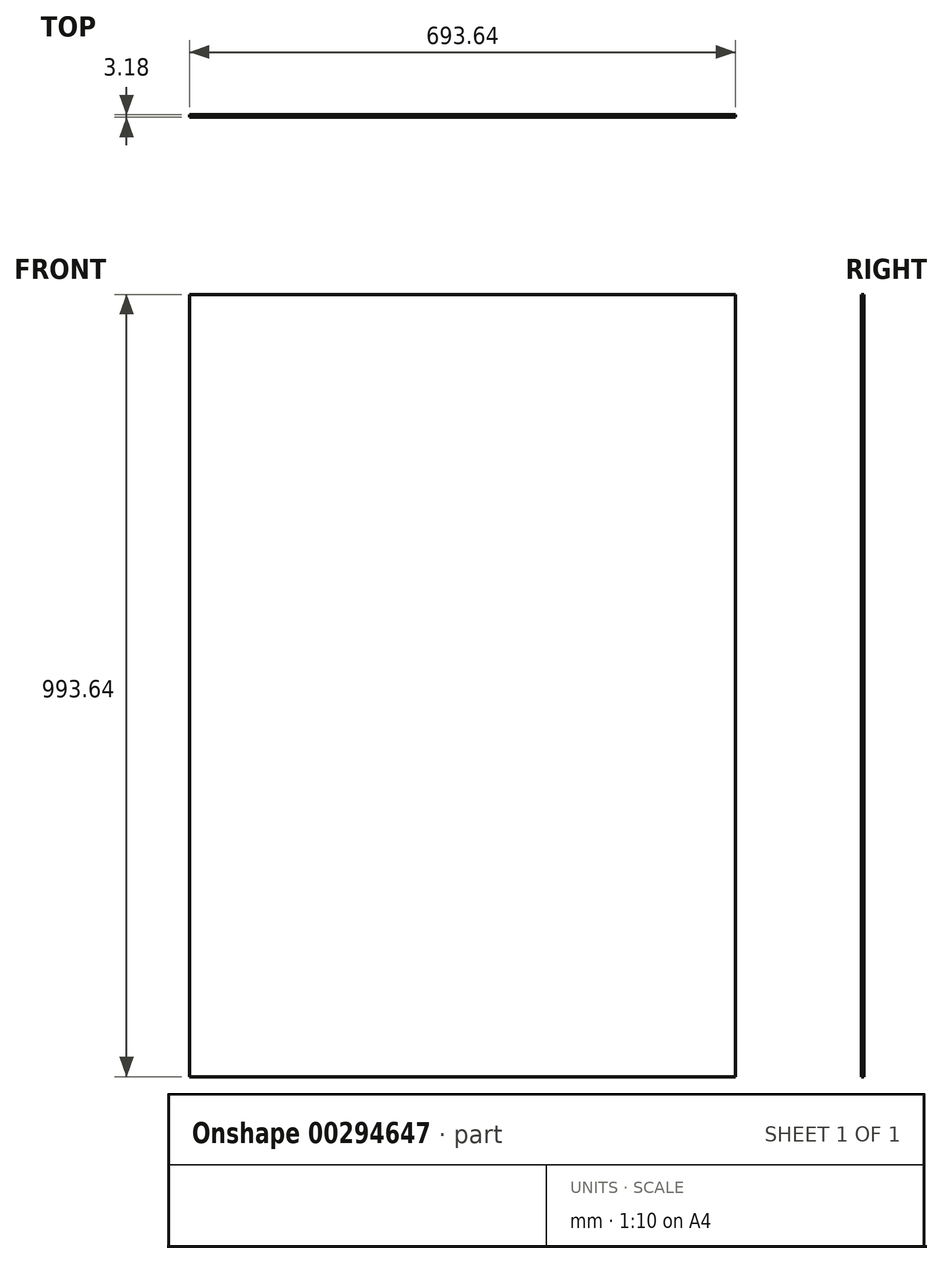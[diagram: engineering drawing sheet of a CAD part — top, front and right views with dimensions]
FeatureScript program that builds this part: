
annotation { "Feature Type Name" : "Feature", "Feature Type Description" : "" }
export const myFeature = defineFeature(function(context is Context, id is Id, definition is map)
    precondition{}
    {
        {
            var Q0;
            Q0=qCreatedBy(makeId("Front.planeOp"),FACE);
            var sketch = newSketch(context, id + "F0", { "sketchPlane" : qUnion([Q0])});
            skLineSegment(sketch, "E0.bottom", {"start": v(346.83, 496.82) * mm, "end": v(-346.82, 496.82) * mm});
            skLineSegment(sketch, "E0.top", {"start": v(346.82, -496.82) * mm, "end": v(-346.83, -496.82) * mm});
            skLineSegment(sketch, "E0.left", {"start": v(346.83, 496.82) * mm, "end": v(346.82, -496.82) * mm});
            skLineSegment(sketch, "E0.right", {"start": v(-346.82, 496.82) * mm, "end": v(-346.83, -496.82) * mm});
            skPoint(sketch, "E0.middle", {"position": v(0, 0) * mm});
            skSolve(sketch);
        }
        {
            var Q0;
            Q0 = qSketchRegion(id + "F0", true);
            extrude(context, id + "F1", {"entities" : qUnion([Q0]), "endBound" : BoundingType.SYMMETRIC, "depth" : 3.17 * mm});
        }
    });
